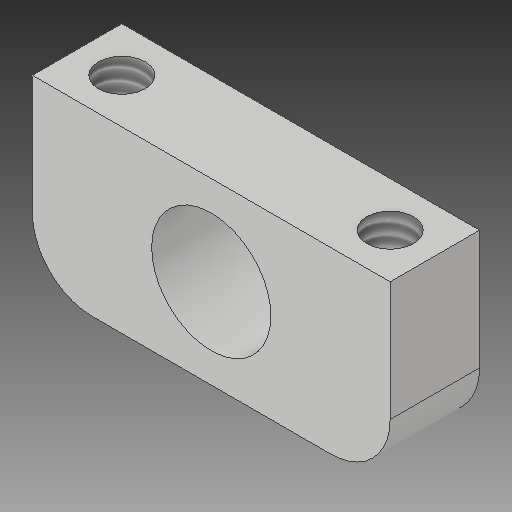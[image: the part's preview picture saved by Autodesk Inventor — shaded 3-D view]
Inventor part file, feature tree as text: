
AUTODESK INVENTOR PART (.ipt)
format: ipt  version: 2017 (Build 210142000, 142)  size: 136,192 bytes
history: native  units: in
note: dims shown in document units (in); Inventor stores cm internally (conversion verified against a paired STEP export)
features: sketch x2, extrude x1, fillet x1, hole x1, mirror x1, projected_geometry x1
ambient origin geometry x8: Origin, YZ Plane, XZ Plane, XY Plane, X Axis, Y Axis, Z Axis, Center Point
bodies: Solid1 (feature_tree)
feature tree (7):
  extrude  "Extrusion1"  Depth=0.75in
  fillet  "Fillet1"  Radius=0.75in
  hole  "Hole1"  [1 undecoded]
  mirror  "Mirror1"
  sketch  "Sketch1"  dims[d0=0.5in d1=0.75in d2=0.75in]
  sketch  "Sketch2"  dims[d3=0.75in d4=0.375in d5=0.0in d6=0.25in d7=0.1875in d9=0.375in d10=0.196in d11=0.4375in d12=0.375in d13=0.25in d14=0.5635in d15=0.4375in d16=0.8108in d17=0.3125in]
  projected_geometry  "Projected Loop1"
note: 1 required parameter value undecoded (feature->parameter linkage not recoverable at this tier; creation-order binding heuristic only, values carry confidence <= 0.55)
